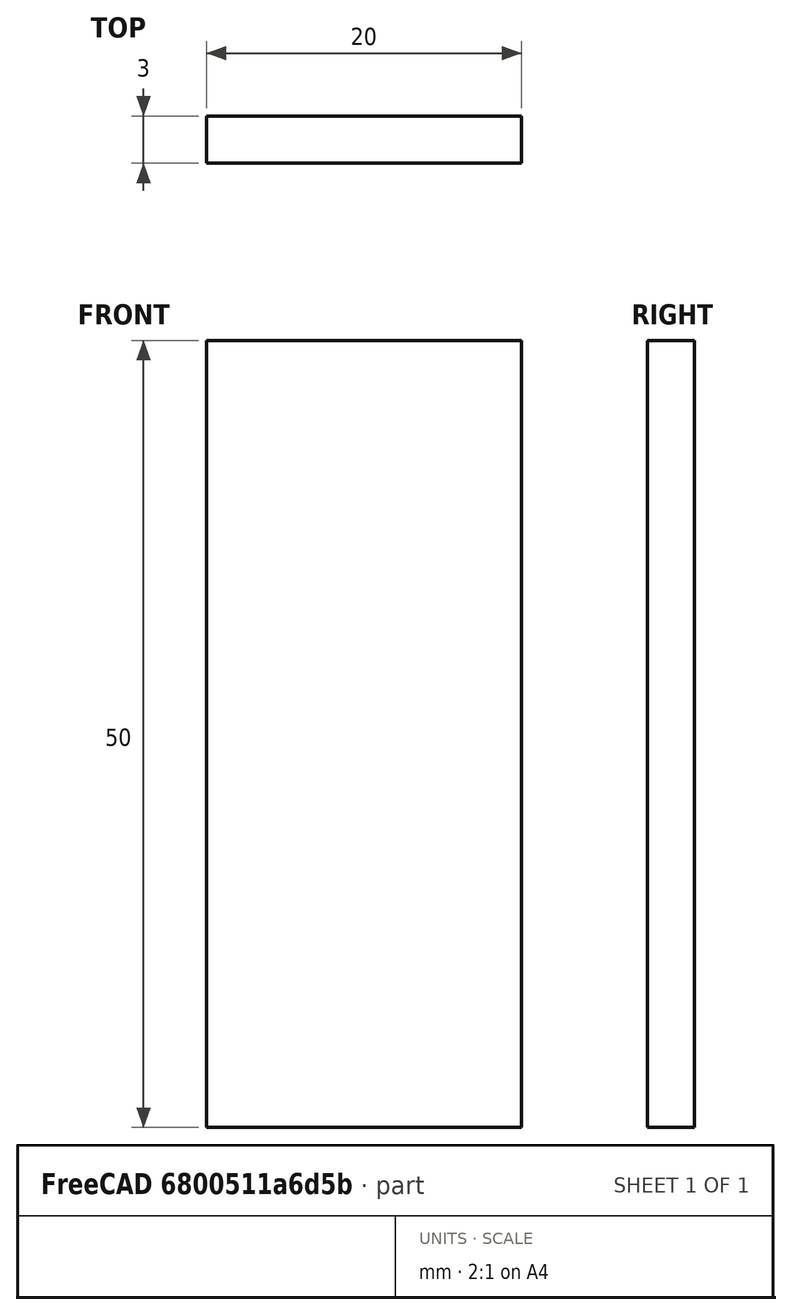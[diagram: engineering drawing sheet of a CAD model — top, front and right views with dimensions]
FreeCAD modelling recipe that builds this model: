
FCSTD DOCUMENT  (FreeCAD 0.15R4671 (Git))
Label: Flat Bar 20x3 EN10058 S235JR
License: All rights reserved
LicenseURL: http://en.wikipedia.org/wiki/All_rights_reserved
objects: Sketcher::SketchObject×1, Part::Extrusion×1
note: 2 computed .brp shape members not serialized (recipe doc carries the construction recipe); baked Part::Feature solids carry a one-line shape summary decoded from their .brp

FEATURE [Sketcher::SketchObject] Sketch
  sketch-geometry (4):
    g0: LineSegment StartX=-10 StartY=-1.5 StartZ=0 EndX=10 EndY=-1.5 EndZ=0
    g1: LineSegment StartX=10 StartY=-1.5 StartZ=0 EndX=10 EndY=1.5 EndZ=0
    g2: LineSegment StartX=10 StartY=1.5 StartZ=0 EndX=-10 EndY=1.5 EndZ=0
    g3: LineSegment StartX=-10 StartY=1.5 StartZ=0 EndX=-10 EndY=-1.5 EndZ=0
  constraints (12):
    c: Coincident(g0,g1)
    c: Coincident(g1,g2)
    c: Coincident(g2,g3)
    c: Coincident(g3,g0)
    c: Horizontal(g0)
    c: Horizontal(g2)
    c: Vertical(g1)
    c: Vertical(g3)
    c: Symmetric(g1,g2,g-2)
    c: Symmetric(g0,g1,g-1)
    c: DistanceY(g1) = 3
    c: DistanceX(g0) = 20
FEATURE [Part::Extrusion] Extrude  label="Flat Bar 20x3 EN10058 S235JR"
  Base = -> Sketch
  Dir = (0,0,50)
  Solid = true
